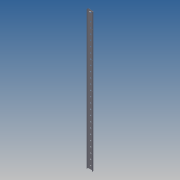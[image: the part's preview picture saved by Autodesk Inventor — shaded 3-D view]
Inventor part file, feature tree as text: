
AUTODESK INVENTOR PART (.ipt)
format: ipt  version: 2011 (Build 150239000, 239)  size: 303,104 bytes
history: native  units: mm
features: fillet x7, extrude x6, sketch x6
ambient origin geometry x8: Origin, YZ Plane, XZ Plane, XY Plane, X Axis, Y Axis, Z Axis, Center Point
feature tree (19):
  extrude  "Extrusion10"  Depth=510.0mm TaperAngle=0.0deg
  extrude  "Extrusion11"  Depth=1.0mm
  extrude  "Extrusion12"  Depth=5.0mm
  fillet  "Fillet12"  Radius=6.799998mm
  fillet  "Fillet13"  Radius=5.0mm
  fillet  "Fillet14"  Radius=6.799998mm
  fillet  "Fillet15"  Radius=4.5mm
  fillet  "Fillet16"  Radius=0.3mm
  fillet  "Fillet17"  Radius=0.3mm
  extrude  "Extrusion13"  Depth=0.1mm
  extrude  "Extrusion14"  Depth=1.0mm
  extrude  "Extrusion15"  Depth=20.0mm
  fillet  "Fillet18"  Radius=12.4mm
  sketch  "Sketch1"  dims[d105=0.1mm d106=510.0mm d107=0.0mm]
  sketch  "Sketch12"  dims[d108=5.3mm d109=1.0mm]
  sketch  "Sketch13"  dims[d110=0.3mm d111=0.0mm d112=5.0mm d113=6.799998mm d115=5.0mm d116=6.799998mm d117=4.5mm d118=0.0mm d119=0.3mm d120=0.3mm]
  sketch  "Sketch14"  dims[d121=0.1mm d122=0.1mm]
  sketch  "Sketch15"  dims[d123=1.0mm d124=1.0mm]
  sketch  "Sketch16"  dims[d137=20.0mm d138=20.0mm d143=12.4mm d144=20.0mm d145=20.0mm d146=20.0mm d147=20.0mm d148=20.0mm d149=20.0mm d150=9.299998mm d151=9.299998mm d152=9.299998mm d153=9.299998mm d154=9.299998mm d155=9.299998mm d156=9.3mm d157=9.3mm d158=9.3mm d159=9.3mm d160=9.3mm d161=9.3mm d162=9.3mm d163=9.3mm d164=9.3mm d165=20.0mm d166=20.0mm d167=20.0mm d168=20.0mm d169=20.0mm d170=20.0mm d171=20.0mm d172=20.0mm d173=20.0mm d174=20.0mm d175=20.0mm d176=20.0mm d177=9.3mm d178=9.300002mm d179=9.3mm d180=9.3mm d181=20.0mm d182=20.0mm d183=9.3mm d184=20.0mm d185=2.0mm d186=0.0mm d193=1.0mm d194=0.0mm d196=5.0mm d198=100.0mm d199=100.0mm d200=100.0mm d201=100.0mm d202=55.0mm d203=1.7mm d204=1.7mm d205=1.7mm d206=1.7mm d207=1.7mm d208=1.7mm d209=1.0mm d210=0.0mm d211=0.1mm]
